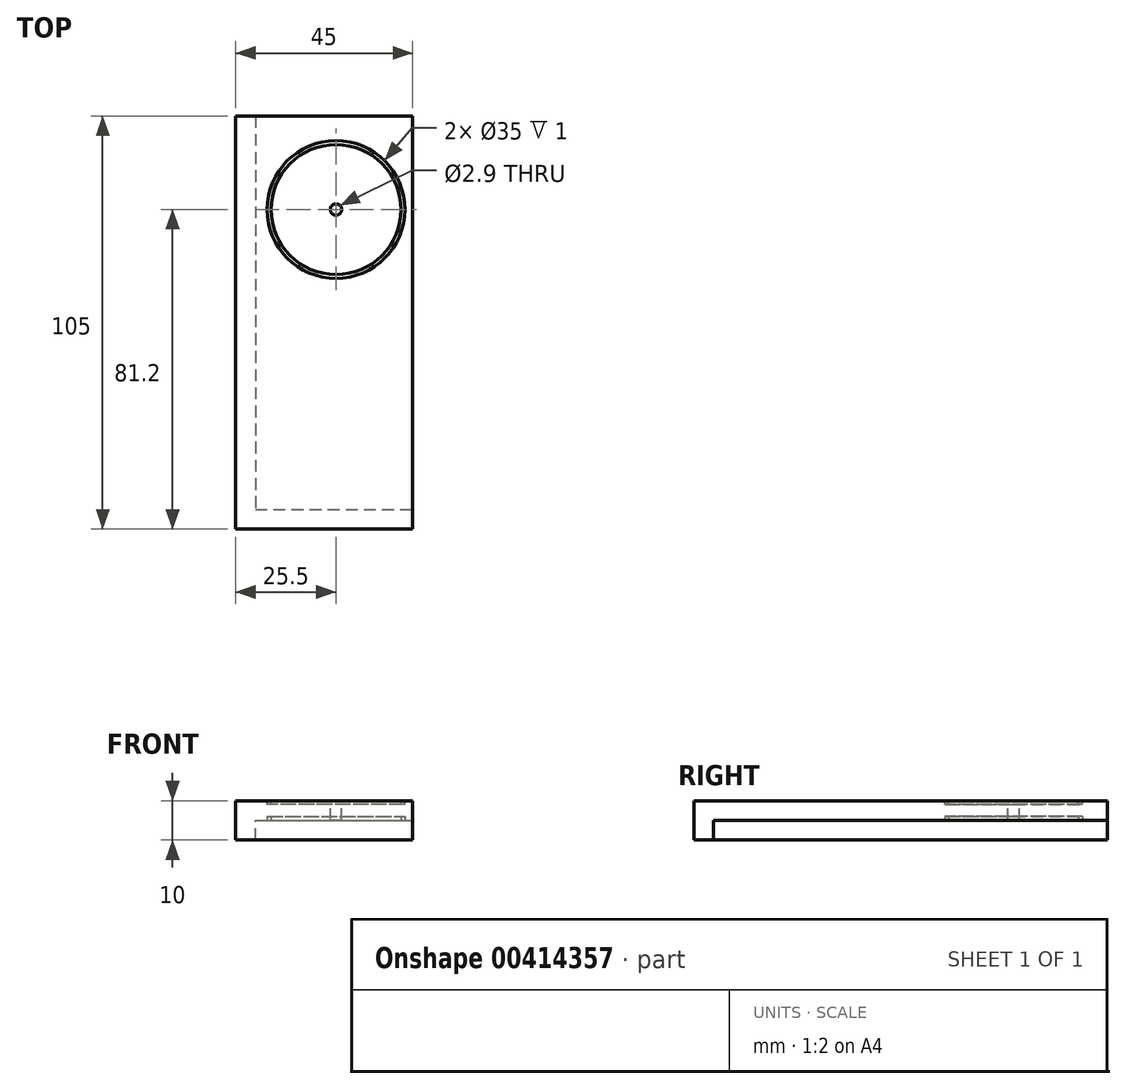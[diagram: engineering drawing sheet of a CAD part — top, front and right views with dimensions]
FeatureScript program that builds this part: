
annotation { "Feature Type Name" : "Feature", "Feature Type Description" : "" }
export const myFeature = defineFeature(function(context is Context, id is Id, definition is map)
    precondition{}
    {
        {
            var Q0;
            Q0=qCreatedBy(makeId("Top.planeOp"),FACE);
            var sketch = newSketch(context, id + "F0", { "sketchPlane" : qUnion([Q0])});
            skLineSegment(sketch, "E0.bottom", {"start": v(-20, 50) * mm, "end": v(20, 50) * mm});
            skLineSegment(sketch, "E0.top", {"start": v(-20, -50) * mm, "end": v(20, -50) * mm});
            skLineSegment(sketch, "E0.left", {"start": v(-20, 50) * mm, "end": v(-20, -50) * mm});
            skLineSegment(sketch, "E0.right", {"start": v(20, 50) * mm, "end": v(20, -50) * mm});
            skPoint(sketch, "E0.middle", {"position": v(0, 0) * mm});
            skCircle(sketch, "E1", {"center": v(0.5, 26.2) * mm, "radius": 17.5 * mm});
            skCircle(sketch, "E2", {"center": v(0.5, 26.2) * mm, "radius": 1.45 * mm});
            skSolve(sketch);
        }
        {
            var Q0;
            Q0=makeQuery(id+"F0.imprint","IMPRINT",FACE,{"disambiguationData":[TD([[makeQuery(id+"F0.imprint","IMPRINT",EDGE,{"derivedFrom":sQuery(id+"F0.wireOp",EDGE,"E0.bottom")}),-1.0]])]});
            var Q1;
            Q1=makeQuery(id+"F0.imprint","IMPRINT",FACE,{"disambiguationData":[TD([[makeQuery(id+"F0.imprint","IMPRINT",EDGE,{"derivedFrom":sQuery(id+"F0.wireOp",EDGE,"E1")}),1.0]])]});
            extrude(context, id + "F1", {"entities" : qUnion([Q0, Q1]), "oppositeDirection" : true, "depth" : 5 * mm});
        }
        {
            var Q0;
            Q0=makeQuery(id+"F0.imprint","IMPRINT",FACE,{"disambiguationData":[TD([[makeQuery(id+"F0.imprint","IMPRINT",EDGE,{"derivedFrom":sQuery(id+"F0.wireOp",EDGE,"E0.bottom")}),-1.0]])]});
            var sketch = newSketch(context, id + "F2", { "sketchPlane" : qUnion([Q0])});
            skLineSegment(sketch, "E3.bottom", {"start": v(-20, -50) * mm, "end": v(-25, -50) * mm});
            skLineSegment(sketch, "E3.top", {"start": v(-20, 50) * mm, "end": v(-25, 50) * mm});
            skLineSegment(sketch, "E3.left", {"start": v(-20, -50) * mm, "end": v(-20, 50) * mm});
            skLineSegment(sketch, "E3.right", {"start": v(-25, -50) * mm, "end": v(-25, 50) * mm});
            skLineSegment(sketch, "E4.bottom", {"start": v(20, -55) * mm, "end": v(-25, -55) * mm});
            skLineSegment(sketch, "E4.top", {"start": v(20, -50) * mm, "end": v(-25, -50) * mm});
            skLineSegment(sketch, "E4.left", {"start": v(20, -55) * mm, "end": v(20, -50) * mm});
            skLineSegment(sketch, "E4.right", {"start": v(-25, -55) * mm, "end": v(-25, -50) * mm});
            skSolve(sketch);
        }
        {
            var Q0;
            Q0=makeQuery(id+"F2.imprint","IMPRINT",FACE,{"disambiguationData":[TD([[makeQuery(id+"F2.imprint","IMPRINT",EDGE,{"derivedFrom":sQuery(id+"F2.wireOp",EDGE,"E3.top")}),1.0]])]});
            var Q1;
            Q1=makeQuery(id+"F2.imprint","IMPRINT",FACE,{"disambiguationData":[TD([[makeQuery(id+"F2.imprint","IMPRINT",EDGE,{"derivedFrom":sQuery(id+"F2.wireOp",EDGE,"E4.bottom")}),-1.0]])]});
            extrude(context, id + "F3", {"entities" : qUnion([Q0, Q1]), "operationType" : NewBodyOperationType.ADD, "oppositeDirection" : true, "depth" : 10 * mm});
        }
        {
            var Q0;
            Q0=makeQuery(id+"F3.boolean.opBoolean","MERGE",FACE,{"derivedFrom":[makeQuery(id+"F1.opExtrude","CAP_FACE",FACE,{"disambiguationData":[OSD([sQuery(id+"F0.wireOp",EDGE,"E0.bottom"),sQuery(id+"F0.wireOp",EDGE,"E0.top"),sQuery(id+"F0.wireOp",EDGE,"E0.left"),sQuery(id+"F0.wireOp",EDGE,"E0.right"),sQuery(id+"F0.wireOp",EDGE,"E2")])],"isStart":true}),makeQuery(id+"F3.opExtrude","CAP_FACE",FACE,{"disambiguationData":[OSD([sQuery(id+"F2.wireOp",EDGE,"E3.bottom"),sQuery(id+"F2.wireOp",EDGE,"E3.left"),sQuery(id+"F2.wireOp",EDGE,"E3.right"),sQuery(id+"F2.wireOp",EDGE,"0Bv1nVha-ZfLD-MYF1-dbGy-8pCfG0kpSLtZ.bottom"),sQuery(id+"F2.wireOp",EDGE,"0Bv1nVha-ZfLD-MYF1-dbGy-8pCfG0kpSLtZ.top"),sQuery(id+"F2.wireOp",EDGE,"0Bv1nVha-ZfLD-MYF1-dbGy-8pCfG0kpSLtZ.left"),sQuery(id+"F2.wireOp",EDGE,"0Bv1nVha-ZfLD-MYF1-dbGy-8pCfG0kpSLtZ.right")])],"isStart":true})]});
            var sketch = newSketch(context, id + "F4", { "sketchPlane" : qUnion([Q0])});
            skCircle(sketch, "E5", {"center": v(0.5, 26.2) * mm, "radius": 17.5 * mm});
            skCircle(sketch, "E6", {"center": v(0.5, 26.2) * mm, "radius": 16.5 * mm});
            skSolve(sketch);
        }
        {
            var Q0;
            Q0=makeQuery(id+"F4.imprint","IMPRINT",FACE,{"disambiguationData":[TD([[makeQuery(id+"F4.imprint","IMPRINT",EDGE,{"derivedFrom":sQuery(id+"F4.wireOp",EDGE,"E5")}),1.0]])]});
            extrude(context, id + "F5", {"entities" : qUnion([Q0]), "operationType" : NewBodyOperationType.REMOVE, "oppositeDirection" : true, "depth" : 1 * mm});
        }
        {
            var Q0;
            Q0=makeQuery(id+"F1.opExtrude","CAP_FACE",FACE,{"disambiguationData":[OSD([sQuery(id+"F0.wireOp",EDGE,"E0.bottom"),sQuery(id+"F0.wireOp",EDGE,"E0.top"),sQuery(id+"F0.wireOp",EDGE,"E0.left"),sQuery(id+"F0.wireOp",EDGE,"E0.right"),sQuery(id+"F0.wireOp",EDGE,"E2")])],"isStart":false});
            var sketch = newSketch(context, id + "F6", { "sketchPlane" : qUnion([Q0])});
            skCircle(sketch, "E7", {"center": v(0.5, -26.2) * mm, "radius": 17.5 * mm});
            skCircle(sketch, "E8", {"center": v(0.5, -26.2) * mm, "radius": 16.5 * mm});
            skSolve(sketch);
        }
        {
            var Q0;
            Q0=makeQuery(id+"F6.imprint","IMPRINT",FACE,{"disambiguationData":[TD([[makeQuery(id+"F6.imprint","IMPRINT",EDGE,{"derivedFrom":sQuery(id+"F6.wireOp",EDGE,"E7")}),1.0]])]});
            extrude(context, id + "F7", {"entities" : qUnion([Q0]), "operationType" : NewBodyOperationType.REMOVE, "oppositeDirection" : true, "depth" : 1 * mm});
        }
    });
